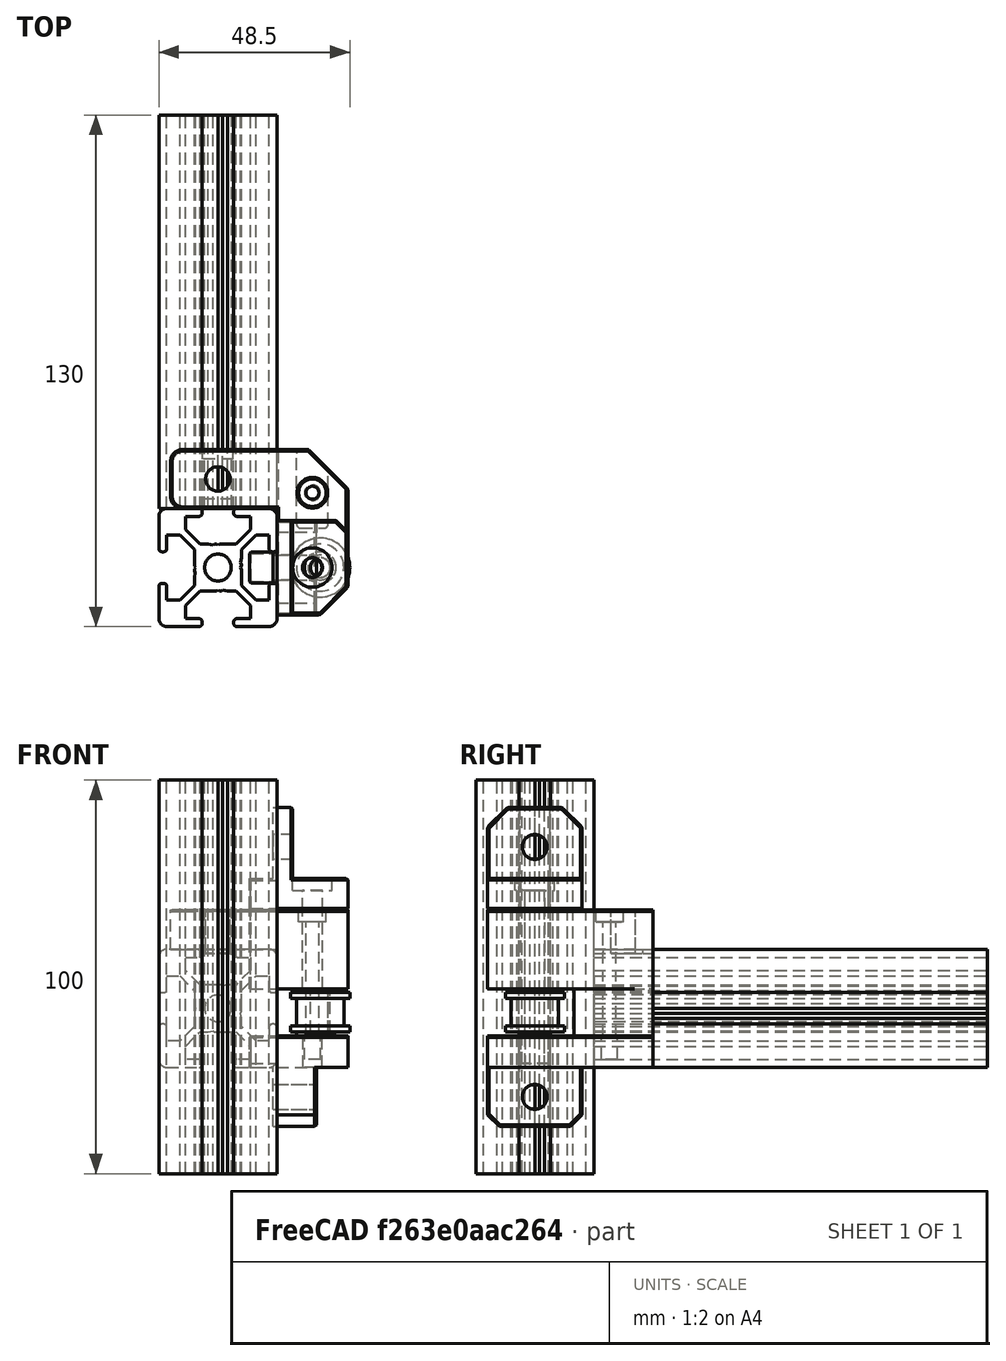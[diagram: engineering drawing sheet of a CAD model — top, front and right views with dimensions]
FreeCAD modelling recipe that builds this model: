
FCSTD DOCUMENT  (FreeCAD 0.19R24291 (Git))
Label: left-idler
License: Other
LicenseURL: GPL3
objects: Part::Chamfer×17, Part::Box×16, Part::Feature×13, Part::Cut×13, Part::Cylinder×10, Part::Fillet×7, Part::MultiFuse×4, Part::Refine×1
note: 81 computed .brp shape members not serialized (recipe doc carries the construction recipe); baked Part::Feature solids carry a one-line shape summary decoded from their .brp

FEATURE [Part::Feature] Extrude001003002002002002  label="Extrude001003002002004"
  Placement = pos=(-15,30,15) rot=(-1,0,0;1.5708rad)
  shape: bbox 30 x 100 x 30 mm, 95 faces (baked)
FEATURE [Part::Feature] Extrude001003002002002001  label="Extrude001003002002003"
  Placement = pos=(-15,15,-27) rot=(0,0,1;0rad)
  shape: bbox 30 x 30 x 100 mm, 95 faces (baked)
FEATURE [Part::Feature] Cut002002  label="smooth-idler-6mm001"
  Placement = pos=(11,15,9) rot=(0,0,-1;1.5708rad)
  shape: bbox 15 x 15 x 10 mm, 8 faces (baked)
FEATURE [Part::Box] Box001  label="Cube001"
  AttacherType = Attacher::AttachEngine3D
  Height = 20
  Length = 18
  Placement = pos=(0,3,20) rot=(0,0,1;0rad)
  Width = 42
FEATURE [Part::Box] Box002  label="Cube002"
  AttacherType = Attacher::AttachEngine3D
  Height = 20
  Length = 7
  Placement = pos=(-7,11.1,20) rot=(0,0,1;0rad)
  Width = 7.8
FEATURE [Part::Box] Box003  label="Cube003"
  AttacherType = Attacher::AttachEngine3D
  Height = 8
  Length = 18
  Placement = pos=(0,3,0) rot=(0,0,1;0rad)
  Width = 42
FEATURE [Part::Box] Box004  label="Cube004"
  AttacherType = Attacher::AttachEngine3D
  Height = 8
  Length = 7
  Placement = pos=(-7,11.1,0) rot=(0,0,1;0rad)
  Width = 7.8
FEATURE [Part::Cylinder] Cylinder001
  Angle = 360
  AttacherType = Attacher::AttachEngine3D
  Height = 35
  Placement = pos=(9,15,13) rot=(0,0,1;0rad)
  Radius = 2.525
FEATURE [Part::Box] Box006  label="Cube006"
  AttacherType = Attacher::AttachEngine3D
  Height = 15
  Length = 10
  Placement = pos=(0,3,-15) rot=(0,0,1;0rad)
  Width = 24
FEATURE [Part::Box] Box011  label="Cube011"
  AttacherType = Attacher::AttachEngine3D
  Height = 10
  Length = 27
  Placement = pos=(-27,30,30) rot=(0,0,1;0rad)
  Width = 15
FEATURE [Part::Chamfer] Chamfer004
  Base = -> Box006
  Edges = 2 edges r=3: [Edge9,Edge11]
FEATURE [Part::Box] Box013  label="Cube013"
  AttacherType = Attacher::AttachEngine3D
  Height = 1
  Length = 7.8
  Placement = pos=(-18.9,30,29) rot=(0,0,1;0rad)
  Width = 15
FEATURE [Part::Cylinder] Cylinder004
  Angle = 360
  AttacherType = Attacher::AttachEngine3D
  Height = 35
  Placement = pos=(9,15,0) rot=(0,0,1;0rad)
  Radius = 2.4
FEATURE [Part::Box] Box015  label="Cube015"
  AttacherType = Attacher::AttachEngine3D
  Height = 12
  Length = 8
  Placement = pos=(7,25,8) rot=(0,0,1;0rad)
  Width = 20
FEATURE [Part::Cylinder] Cylinder005
  Angle = 360
  AttacherType = Attacher::AttachEngine3D
  Height = 40
  Placement = pos=(9,34,3) rot=(0,0,1;0rad)
  Radius = 1.65
FEATURE [Part::Cylinder] Cylinder006
  Angle = 360
  AttacherType = Attacher::AttachEngine3D
  Height = 10
  Placement = pos=(9,34,37) rot=(0,0,1;0rad)
  Radius = 3.5
FEATURE [Part::Cylinder] Cylinder008
  Angle = 360
  AttacherType = Attacher::AttachEngine3D
  Height = 16
  Placement = pos=(-2,15,-7.5) rot=(0,1,0;1.5708rad)
  Radius = 3.15
FEATURE [Part::Chamfer] Chamfer009
  Base = -> Box015
  Edges = 1 edges r=5: [Edge7]
FEATURE [Part::Chamfer] Chamfer010
  Base = -> Box004
  Edges = 2 edges r=0.4: [Edge1,Edge3]
FEATURE [Part::Chamfer] Chamfer011
  Base = -> Box002
  Edges = 2 edges r=0.4: [Edge1,Edge3]
FEATURE [Part::Fillet] Fillet001
  Base = -> Chamfer009
  Edges = 4 edges r=1: [Edge2,Edge3,Edge12,Edge15]
  Placement = pos=(-2,0,0) rot=(0,0,1;0rad)
FEATURE [Part::Cylinder] Cylinder011
  Angle = 360
  AttacherType = Attacher::AttachEngine3D
  Height = 40
  Placement = pos=(9,34,2) rot=(0,0,1;0rad)
  Radius = 2
FEATURE [Part::Feature] Cut002002002001  label="idler-washer001"
  Placement = pos=(11,15,8) rot=(0,0,1;0rad)
  shape: bbox 8 x 8 x 0.85 mm, 4 faces (baked)
FEATURE [Part::Feature] Cut002002002002  label="idler-washer002"
  Placement = pos=(11,15,20) rot=(0,1,0;3.14159rad)
  shape: bbox 8 x 8 x 0.85 mm, 4 faces (baked)
FEATURE [Part::Chamfer] Chamfer013
  Base = -> Box001
  Edges = 1 edges r=7: [Edge5]
FEATURE [Part::Fillet] Fillet
  Base = -> Box011
  Edges = 2 edges r=3: [Edge1,Edge3]
FEATURE [Part::MultiFuse] Fusion
  Shapes = -> [Fillet,Box013]
FEATURE [Part::Box] Box  label="Cube"
  AttacherType = Attacher::AttachEngine3D
  Height = 15
  Length = 1
  Placement = pos=(-1,11.1,-15) rot=(0,0,1;0rad)
  Width = 7.8
FEATURE [Part::Chamfer] Chamfer
  Base = -> Box003
  Edges = 1 edges r=7: [Edge5]
FEATURE [Part::Chamfer] Chamfer015
  Base = -> Chamfer
  Edges = 1 edges r=10: [Edge3]
FEATURE [Part::Chamfer] Chamfer016
  Base = -> Chamfer013
  Edges = 1 edges r=10: [Edge3]
FEATURE [Part::Fillet] Fillet002
  Base = -> Chamfer016
  Edges = 4 edges r=1: [Edge2,Edge3,Edge11,Edge13]
FEATURE [Part::Fillet] Fillet003
  Base = -> Fillet001
  Edges = 1 edges r=1: [Edge24]
FEATURE [Part::Fillet] Fillet004
  Base = -> Chamfer015
  Edges = 4 edges r=1: [Edge2,Edge3,Edge11,Edge13]
FEATURE [Part::Chamfer] Chamfer017
  Base = -> Chamfer004
  Edges = 5 edges r=0.4: [Edge7,Edge11,Edge15,Edge16,Edge18]
FEATURE [Part::MultiFuse] Fusion006003
  Shapes = -> [Box,Chamfer017,Chamfer010,Fillet004]
FEATURE [Part::Cut] Cut002002002003
  Base = -> Fusion006003
  Tool = -> Cylinder008
FEATURE [Part::Cut] Cut002002002006
  Base = -> Cut002002002003
  Tool = -> Cylinder011
FEATURE [Part::Cut] Cut002002002007
  Base = -> Cut002002002006
  Tool = -> Cylinder004
FEATURE [Part::Feature] Cut002002002007001  label="Cut002002002010"
  shape: bbox 25 x 42 x 23 mm, 35 faces (baked)
FEATURE [Part::Chamfer] Chamfer019  label="btm-exp"
  Base = -> Cut002002002007001
  Edges = 16 edges r=0.4: [Edge13,Edge17,Edge19,Edge62,Edge65,Edge67,Edge69,Edge73,Edge75,Edge77,Edge78,Edge81,Edge85,Edge88,Edge89,Edge90]
FEATURE [Part::Cylinder] Cylinder
  Angle = 360
  AttacherType = Attacher::AttachEngine3D
  Height = 15
  Placement = pos=(-15,37.5,27) rot=(0,0,1;0rad)
  Radius = 3.1
FEATURE [Part::MultiFuse] Fusion006004
  Shapes = -> [Fusion,Fillet002,Chamfer011,Fillet003]
FEATURE [Part::Cut] Cut
  Base = -> Fusion006004
  Tool = -> Cylinder
FEATURE [Part::Cut] Cut002002002007002
  Base = -> Cut
  Tool = -> Cylinder006
FEATURE [Part::Cut] Cut002002002007003
  Base = -> Cut002002002007002
  Tool = -> Cylinder001
FEATURE [Part::Cut] Cut002002002007004
  Base = -> Cut002002002007003
  Tool = -> Cylinder005
FEATURE [Part::Feature] Cut002002002007004001  label="Cut002002002007005"
  shape: bbox 45 x 42 x 32 mm, 40 faces (baked)
FEATURE [Part::Chamfer] Chamfer020  label="top-exp"
  Base = -> Cut002002002007004001
  Edges = 21 edges r=0.4: [Edge1,Edge7,Edge8,Edge14,Edge17,Edge20,Edge23,Edge26,Edge27,Edge31,Edge34,Edge39,Edge47,Edge53,Edge56,Edge69,Edge70,Edge71,Edge72,Edge73,Edge74]
FEATURE [Part::Box] Box016  label="Cube016"
  AttacherType = Attacher::AttachEngine3D
  Height = 26
  Length = 4
  Placement = pos=(0,3,40) rot=(0,0,1;0rad)
  Width = 24
FEATURE [Part::Box] Box017  label="Cube017"
  AttacherType = Attacher::AttachEngine3D
  Height = 8
  Length = 8
  Placement = pos=(-7,11.1,40) rot=(0,0,1;0rad)
  Width = 7.8
FEATURE [Part::Box] Box018  label="Cube018"
  AttacherType = Attacher::AttachEngine3D
  Height = 8
  Length = 18
  Placement = pos=(0,3,40) rot=(0,0,1;0rad)
  Width = 24
FEATURE [Part::Cylinder] Cylinder012
  Angle = 360
  AttacherType = Attacher::AttachEngine3D
  Height = 35
  Placement = pos=(9,15,32.7) rot=(0,0,1;0rad)
  Radius = 2.525
FEATURE [Part::Cylinder] Cylinder013
  Angle = 360
  AttacherType = Attacher::AttachEngine3D
  Height = 5
  Placement = pos=(9,15,45) rot=(0,0,1;0rad)
  Radius = 5
FEATURE [Part::Chamfer] Chamfer021
  Base = -> Box018
  Edges = 1 edges r=7: [Edge5]
FEATURE [Part::Chamfer] Chamfer022
  Base = -> Chamfer021
  Edges = 1 edges r=3: [Edge4]
FEATURE [Part::Fillet] Fillet005
  Base = -> Chamfer022
  Edges = 4 edges r=1: [Edge2,Edge4,Edge11,Edge13]
FEATURE [Part::Chamfer] Chamfer023
  Base = -> Fillet005
  Edges = 20 edges r=0.4: [Edge1,Edge3,Edge5,Edge6,Edge7,Edge8,Edge9,Edge10,Edge11,Edge12,Edge13,Edge14,Edge16,Edge18,Edge19,Edge20,Edge21,Edge22,Edge23,Edge24]
FEATURE [Part::Cut] Cut002002002007004002
  Base = -> Chamfer023
  Tool = -> Cylinder013
FEATURE [Part::Cut] Cut002002002007004003
  Base = -> Cut002002002007004002
  Tool = -> Cylinder012
FEATURE [Part::Box] Box019  label="Cube019"
  AttacherType = Attacher::AttachEngine3D
  Height = 18
  Length = 2
  Placement = pos=(-1,11.1,48) rot=(0,0,1;0rad)
  Width = 7.8
FEATURE [Part::Cylinder] Cylinder014
  Angle = 360
  AttacherType = Attacher::AttachEngine3D
  Height = 15
  Placement = pos=(9,15,56) rot=(0.57735,-0.57735,-0.57735;2.0944rad)
  Radius = 3.15
FEATURE [Part::Chamfer] Chamfer024
  Base = -> Box016
  Edges = 2 edges r=5: [Edge10,Edge12]
FEATURE [Part::Fillet] Fillet006
  Base = -> Chamfer024
  Edges = 4 edges r=1: [Edge9,Edge11,Edge15,Edge17]
FEATURE [Part::Chamfer] Chamfer025
  Base = -> Fillet006
  Edges = 13 edges r=0.4: [Edge2,Edge11,Edge12,Edge15,Edge16,Edge17,Edge18,Edge20,Edge23,Edge25,Edge26,Edge28,Edge30]
FEATURE [Part::Chamfer] Chamfer026
  Base = -> Box017
  Edges = 5 edges r=0.4: [Edge1,Edge3,Edge4,Edge9,Edge11]
FEATURE [Part::MultiFuse] Fusion006005
  Shapes = -> [Chamfer026,Chamfer025,Cut002002002007004003,Box019]
FEATURE [Part::Cut] Cut002002002007004004  label="top-support"
  Base = -> Fusion006005
  Tool = -> Cylinder014
FEATURE [Part::Refine] Cut002002002007004004001  label="top-support-exp"
  Source = -> Cut002002002007004004
FEATURE [Part::Box] Box020  label="Cube020"
  AttacherType = Attacher::AttachEngine3D
  Height = 10
  Length = 10
  Placement = pos=(-20,32.5,20) rot=(0,0,1;0rad)
  Width = 10
FEATURE [Part::Box] Box021  label="Cube021"
  AttacherType = Attacher::AttachEngine3D
  Height = 19
  Length = 10
  Placement = pos=(-10,10,47.5) rot=(0,0,1;0rad)
  Width = 10
FEATURE [Part::Box] Box022  label="Cube022"
  AttacherType = Attacher::AttachEngine3D
  Height = 17
  Length = 10
  Placement = pos=(-10,10,-16) rot=(0,0,1;0rad)
  Width = 10
FEATURE [Part::Feature] Cut002002002007004004001001  label="top-support-exp001"
  shape: bbox 25 x 24 x 26 mm, 66 faces (baked)
FEATURE [Part::Feature] Chamfer020001  label="top-exp001"
  shape: bbox 45 x 42 x 32 mm, 61 faces (baked)
FEATURE [Part::Feature] Chamfer019001  label="btm-exp001"
  shape: bbox 25 x 42 x 23 mm, 51 faces (baked)
FEATURE [Part::Cut] Cut002002002007004004001003  label="top-trim"
  Base = -> Chamfer020001
  Tool = -> Box020
FEATURE [Part::Cut] Cut002002002007004004001005  label="top-support-trim"
  Base = -> Cut002002002007004004001001
  Tool = -> Box021
FEATURE [Part::Cut] Cut002002002007004004001006  label="bottom-trim"
  Base = -> Chamfer019001
  Tool = -> Box022
FEATURE [Part::Feature] Cut002002002007004004001006001001  label="bottom-trim002"
  shape: bbox 25 x 42 x 23 mm, 49 faces (baked)
FEATURE [Part::Feature] Cut002002002007004004001003001001  label="top-trim002"
  shape: bbox 45 x 42 x 32 mm, 65 faces (baked)
FEATURE [Part::Feature] Cut002002002007004004001005001001  label="top-support-trim002"
  shape: bbox 25 x 24 x 26 mm, 64 faces (baked)
